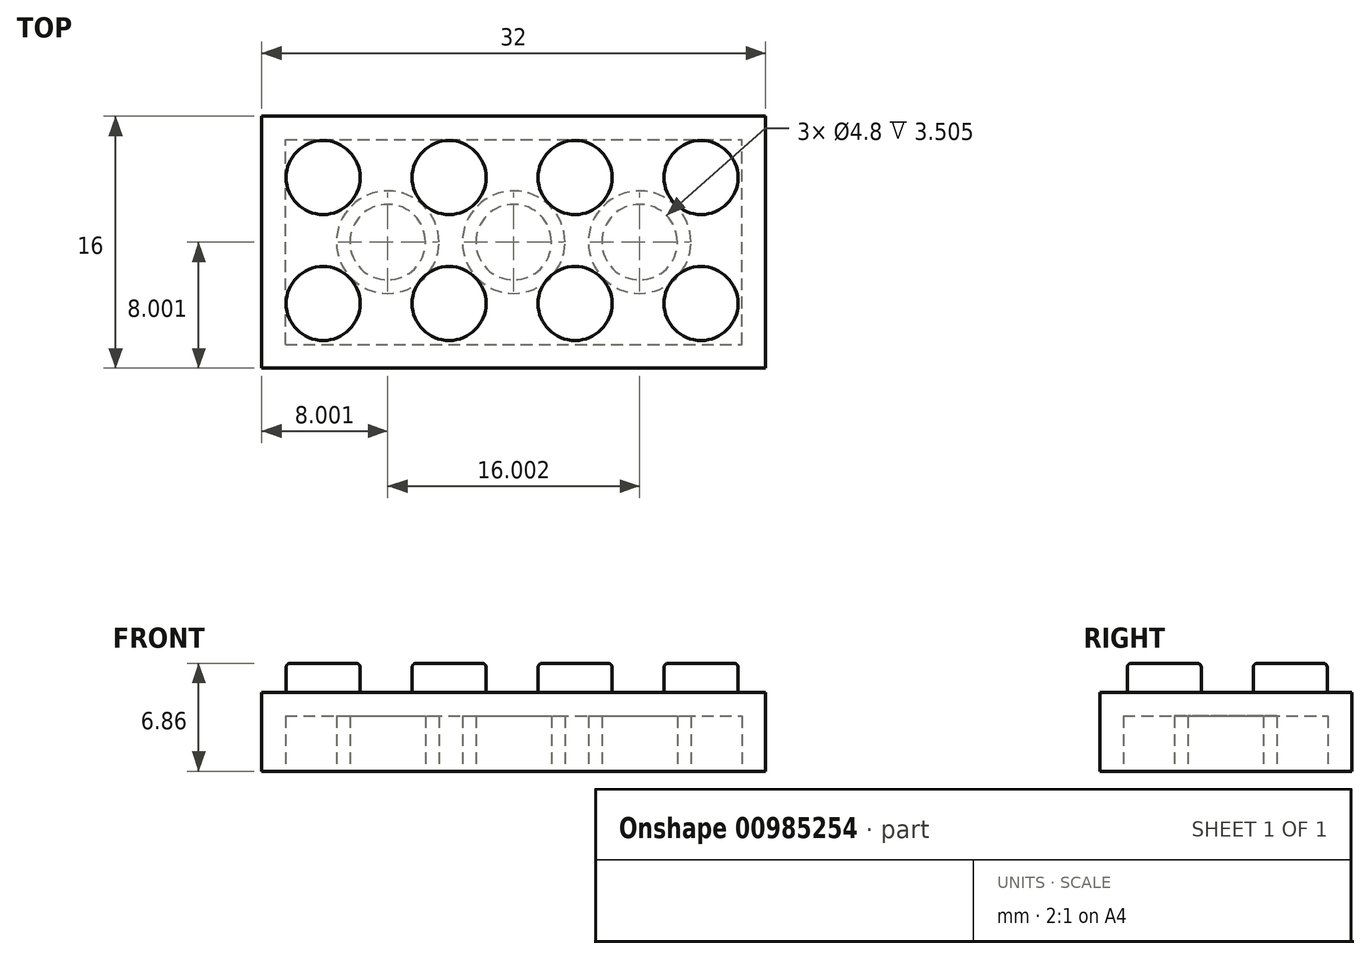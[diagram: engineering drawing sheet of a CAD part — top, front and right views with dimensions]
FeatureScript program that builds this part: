
annotation { "Feature Type Name" : "Feature", "Feature Type Description" : "" }
export const myFeature = defineFeature(function(context is Context, id is Id, definition is map)
    precondition{}
    {
        {
            var Q0;
            Q0=qCreatedBy(makeId("Top.planeOp"),FACE);
            var sketch = newSketch(context, id + "F0", { "sketchPlane" : qUnion([Q0])});
            skLineSegment(sketch, "E0.bottom", {"start": v(0, 0) * mm, "end": v(32, 0) * mm});
            skLineSegment(sketch, "E0.top", {"start": v(0, 16) * mm, "end": v(32, 16) * mm});
            skLineSegment(sketch, "E0.left", {"start": v(0, 0) * mm, "end": v(0, 16) * mm});
            skLineSegment(sketch, "E0.right", {"start": v(32, 0) * mm, "end": v(32, 16) * mm});
            skSolve(sketch);
        }
        {
            var Q0;
            Q0=makeQuery(id+"F0.imprint","IMPRINT",FACE,{"disambiguationData":[TD([[makeQuery(id+"F0.imprint","IMPRINT",EDGE,{"derivedFrom":sQuery(id+"F0.wireOp",EDGE,"E0.bottom")}),1.0]])]});
            extrude(context, id + "F1", {"entities" : qUnion([Q0]), "depth" : 5 * mm, "offsetDistance" : 25.4 * mm});
        }
        {
            var Q0;
            Q0=makeQuery(id+"F1.opExtrude","CAP_FACE",FACE,{"disambiguationData":[OSD([sQuery(id+"F0.wireOp",EDGE,"E0.bottom"),sQuery(id+"F0.wireOp",EDGE,"E0.top"),sQuery(id+"F0.wireOp",EDGE,"E0.left"),sQuery(id+"F0.wireOp",EDGE,"E0.right")])],"isStart":false});
            var sketch = newSketch(context, id + "F2", { "sketchPlane" : qUnion([Q0])});
            skCircle(sketch, "E1", {"center": v(3.9, 12.1) * mm, "radius": 2.35 * mm});
            skCircle(sketch, "E2.0.1.0", {"center": v(3.9, 4.1) * mm, "radius": 2.35 * mm});
            skCircle(sketch, "E2.1.0.0", {"center": v(11.9, 12.1) * mm, "radius": 2.35 * mm});
            skCircle(sketch, "E2.1.1.0", {"center": v(11.9, 4.1) * mm, "radius": 2.35 * mm});
            skCircle(sketch, "E2.2.0.0", {"center": v(19.9, 12.1) * mm, "radius": 2.35 * mm});
            skCircle(sketch, "E2.2.1.0", {"center": v(19.9, 4.1) * mm, "radius": 2.35 * mm});
            skCircle(sketch, "E2.3.0.0", {"center": v(27.9, 12.1) * mm, "radius": 2.35 * mm});
            skCircle(sketch, "E2.3.1.0", {"center": v(27.9, 4.1) * mm, "radius": 2.35 * mm});
            skLineSegment(sketch, "E2.direction1", {"start": v(3.9, 12.1) * mm, "end": v(11.9, 12.1) * mm, "construction": true});
            skLineSegment(sketch, "E2.direction2", {"start": v(3.9, 12.1) * mm, "end": v(3.9, 4.1) * mm, "construction": true});
            skSolve(sketch);
        }
        {
            var Q0;
            Q0=makeQuery(id+"F2.imprint","IMPRINT",FACE,{"disambiguationData":[TD([[makeQuery(id+"F2.imprint","IMPRINT",EDGE,{"derivedFrom":sQuery(id+"F2.wireOp",EDGE,"E2.0.1.0")}),1.0]])]});
            var Q1;
            Q1=makeQuery(id+"F2.imprint","IMPRINT",FACE,{"disambiguationData":[TD([[makeQuery(id+"F2.imprint","IMPRINT",EDGE,{"derivedFrom":sQuery(id+"F2.wireOp",EDGE,"E2.1.1.0")}),1.0]])]});
            var Q2;
            Q2=makeQuery(id+"F2.imprint","IMPRINT",FACE,{"disambiguationData":[TD([[makeQuery(id+"F2.imprint","IMPRINT",EDGE,{"derivedFrom":sQuery(id+"F2.wireOp",EDGE,"E2.2.1.0")}),1.0]])]});
            var Q3;
            Q3=makeQuery(id+"F2.imprint","IMPRINT",FACE,{"disambiguationData":[TD([[makeQuery(id+"F2.imprint","IMPRINT",EDGE,{"derivedFrom":sQuery(id+"F2.wireOp",EDGE,"E1")}),1.0]])]});
            var Q4;
            Q4=makeQuery(id+"F2.imprint","IMPRINT",FACE,{"disambiguationData":[TD([[makeQuery(id+"F2.imprint","IMPRINT",EDGE,{"derivedFrom":sQuery(id+"F2.wireOp",EDGE,"E2.1.0.0")}),1.0]])]});
            var Q5;
            Q5=makeQuery(id+"F2.imprint","IMPRINT",FACE,{"disambiguationData":[TD([[makeQuery(id+"F2.imprint","IMPRINT",EDGE,{"derivedFrom":sQuery(id+"F2.wireOp",EDGE,"E2.2.0.0")}),1.0]])]});
            var Q6;
            Q6=makeQuery(id+"F2.imprint","IMPRINT",FACE,{"disambiguationData":[TD([[makeQuery(id+"F2.imprint","IMPRINT",EDGE,{"derivedFrom":sQuery(id+"F2.wireOp",EDGE,"E2.3.0.0")}),1.0]])]});
            var Q7;
            Q7=makeQuery(id+"F2.imprint","IMPRINT",FACE,{"disambiguationData":[TD([[makeQuery(id+"F2.imprint","IMPRINT",EDGE,{"derivedFrom":sQuery(id+"F2.wireOp",EDGE,"E2.3.1.0")}),1.0]])]});
            extrude(context, id + "F3", {"entities" : qUnion([Q0, Q1, Q2, Q3, Q4, Q5, Q6, Q7]), "operationType" : NewBodyOperationType.ADD, "depth" : 1.85 * mm, "offsetDistance" : 25.4 * mm});
        }
        {
            var Q0;
            Q0=makeQuery(id+"F3.opExtrude","CAP_EDGE",EDGE,{"disambiguationData":[OSD([sQuery(id+"F2.wireOp",EDGE,"E2.0.1.0")])],"isStart":false});
            var Q1;
            Q1=makeQuery(id+"F3.opExtrude","CAP_EDGE",EDGE,{"disambiguationData":[OSD([sQuery(id+"F2.wireOp",EDGE,"E2.1.1.0")])],"isStart":false});
            var Q2;
            Q2=makeQuery(id+"F3.opExtrude","CAP_EDGE",EDGE,{"disambiguationData":[OSD([sQuery(id+"F2.wireOp",EDGE,"E2.2.1.0")])],"isStart":false});
            var Q3;
            Q3=makeQuery(id+"F3.opExtrude","CAP_EDGE",EDGE,{"disambiguationData":[OSD([sQuery(id+"F2.wireOp",EDGE,"E2.3.1.0")])],"isStart":false});
            var Q4;
            Q4=makeQuery(id+"F3.opExtrude","CAP_EDGE",EDGE,{"disambiguationData":[OSD([sQuery(id+"F2.wireOp",EDGE,"E2.3.0.0")])],"isStart":false});
            var Q5;
            Q5=makeQuery(id+"F3.opExtrude","CAP_EDGE",EDGE,{"disambiguationData":[OSD([sQuery(id+"F2.wireOp",EDGE,"E2.2.0.0")])],"isStart":false});
            var Q6;
            Q6=makeQuery(id+"F3.opExtrude","CAP_EDGE",EDGE,{"disambiguationData":[OSD([sQuery(id+"F2.wireOp",EDGE,"E2.1.0.0")])],"isStart":false});
            var Q7;
            Q7=makeQuery(id+"F3.opExtrude","CAP_EDGE",EDGE,{"disambiguationData":[OSD([sQuery(id+"F2.wireOp",EDGE,"E1")])],"isStart":false});
            fillet(context, id + "F4", {"entities" : qUnion([Q0, Q1, Q2, Q3, Q4, Q5, Q6, Q7]), "radius" : 0.25 * mm, "tangentPropagation" : true, "allowEdgeOverflow" : false});
        }
        {
            var Q0;
            Q0=makeQuery(id+"F1.opExtrude","CAP_FACE",FACE,{"disambiguationData":[OSD([sQuery(id+"F0.wireOp",EDGE,"E0.bottom"),sQuery(id+"F0.wireOp",EDGE,"E0.top"),sQuery(id+"F0.wireOp",EDGE,"E0.left"),sQuery(id+"F0.wireOp",EDGE,"E0.right")])],"isStart":true});
            var sketch = newSketch(context, id + "F5", { "sketchPlane" : qUnion([Q0])});
            skLineSegment(sketch, "E3.0", {"start": v(1.5, -1.5) * mm, "end": v(1.5, -14.5) * mm});
            skLineSegment(sketch, "E3.1", {"start": v(1.5, -1.5) * mm, "end": v(30.5, -1.5) * mm});
            skLineSegment(sketch, "E3.2", {"start": v(30.5, -1.5) * mm, "end": v(30.5, -14.5) * mm});
            skLineSegment(sketch, "E3.3", {"start": v(1.5, -14.5) * mm, "end": v(30.5, -14.5) * mm});
            skLineSegment(sketch, "E4", {"start": v(0, 0) * mm, "end": v(32, -16) * mm, "construction": true});
            skLineSegment(sketch, "E5", {"start": v(32, -16) * mm, "end": v(32, 0) * mm});
            skLineSegment(sketch, "E6", {"start": v(32, 0) * mm, "end": v(0, -16) * mm, "construction": true});
            skCircle(sketch, "E7", {"center": v(16, -8) * mm, "radius": 3.25 * mm});
            skCircle(sketch, "E8", {"center": v(16, -8) * mm, "radius": 2.4 * mm});
            skCircle(sketch, "E9", {"center": v(24, -8) * mm, "radius": 2.4 * mm});
            skCircle(sketch, "E10", {"center": v(24, -8) * mm, "radius": 3.25 * mm});
            skCircle(sketch, "E11", {"center": v(8, -8) * mm, "radius": 2.4 * mm});
            skCircle(sketch, "E12", {"center": v(8, -8) * mm, "radius": 3.25 * mm});
            skSolve(sketch);
        }
        {
            var Q0;
            Q0=makeQuery(id+"F5.imprint","IMPRINT",FACE,{"disambiguationData":[TD([[makeQuery(id+"F5.imprint","IMPRINT",EDGE,{"derivedFrom":sQuery(id+"F5.wireOp",EDGE,"E3.0")}),1.0]])]});
            var Q1;
            Q1=makeQuery(id+"F5.imprint","IMPRINT",FACE,{"disambiguationData":[TD([[makeQuery(id+"F5.imprint","IMPRINT",EDGE,{"derivedFrom":sQuery(id+"F5.wireOp",EDGE,"E9")}),1.0]])]});
            var Q2;
            Q2=makeQuery(id+"F5.imprint","IMPRINT",FACE,{"disambiguationData":[TD([[makeQuery(id+"F5.imprint","IMPRINT",EDGE,{"derivedFrom":sQuery(id+"F5.wireOp",EDGE,"E8")}),1.0]])]});
            var Q3;
            Q3=makeQuery(id+"F5.imprint","IMPRINT",FACE,{"disambiguationData":[TD([[makeQuery(id+"F5.imprint","IMPRINT",EDGE,{"derivedFrom":sQuery(id+"F5.wireOp",EDGE,"E11")}),1.0]])]});
            extrude(context, id + "F6", {"entities" : qUnion([Q0, Q1, Q2, Q3]), "operationType" : NewBodyOperationType.REMOVE, "oppositeDirection" : true, "depth" : 3.5 * mm, "offsetDistance" : 25.4 * mm});
        }
    });
